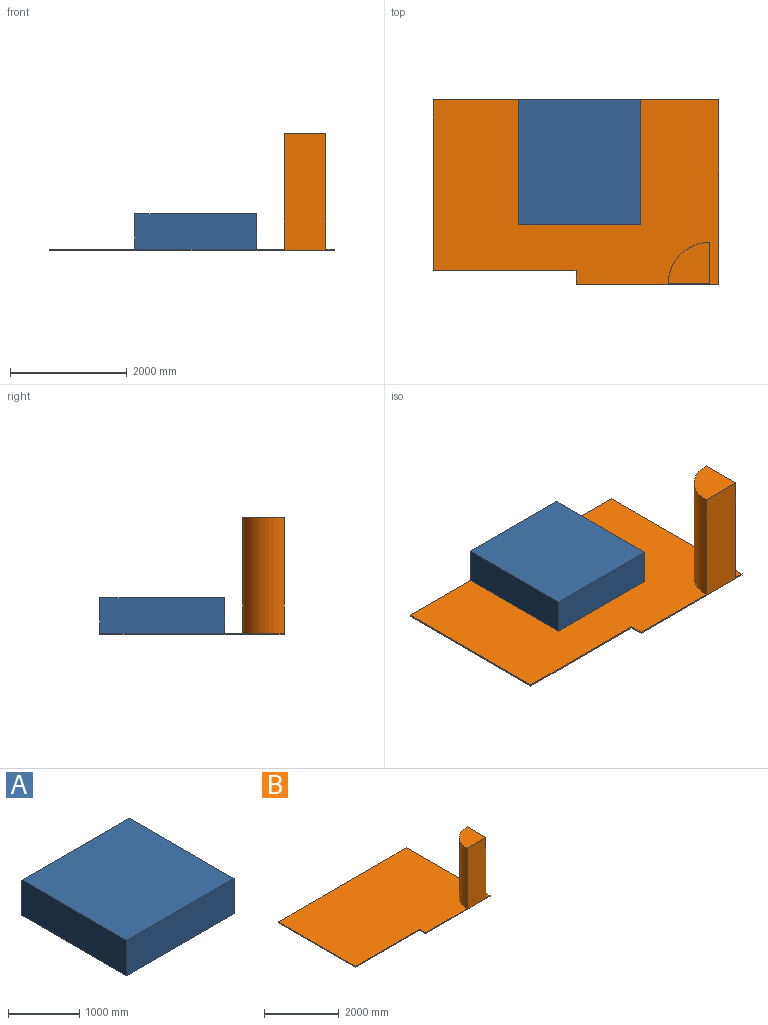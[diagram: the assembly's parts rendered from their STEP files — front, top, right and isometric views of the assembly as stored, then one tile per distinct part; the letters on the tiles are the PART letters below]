
ASSEMBLY  parts=2 mates=2
PART A: 6 faces, bbox 2133.6x2082.8x609.6 mm
  f0: plane 2133.6x609.6mm, normal (0,-1,0), area 1300642.6mm2, adj f1,f3,f4,f5
  f1: plane 2082.8x609.6mm, normal (1,0,0), area 1269674.9mm2, adj f0,f2,f4,f5
  f2: plane 2133.6x609.6mm, normal (0,1,0), area 1300642.6mm2, adj f1,f3,f4,f5
  f3: plane 2082.8x609.6mm, normal (-1,0,0), area 1269674.9mm2, adj f0,f2,f4,f5
  f4: plane 2133.6x2082.8mm, normal (0,0,1), area 4443862.1mm2, adj f0,f1,f2,f3
  f5: plane 2133.6x2082.8mm, normal (0,0,-1), area 4443862.1mm2, adj f0,f1,f2,f3
PART B: 11 faces, bbox 4876.8x3149.6x2006.2 mm
  f0: plane 2921x25mm, normal (-1,0,0), area 73025mm2, adj f1,f5,f6,f7
  f1: plane 2438.4x25mm, normal (0,-1,0), area 60960mm2, adj f0,f2,f6,f7
  f2: plane 228.6x25mm, normal (-1,0,0), area 5715mm2, adj f1,f3,f6,f7
  f3: plane 2438.4x2006.2mm, normal (0,-1,0), area 1469989.4mm2, adj f2,f4,f6,f7,f8,f9,f10
  f4: plane 3149.6x25mm, normal (1,0,0), area 78740mm2, adj f3,f5,f6,f7
  f5: plane 4876.8x25mm, normal (0,1,0), area 121920mm2, adj f0,f4,f6,f7
  f6: plane 4876.8x3149.6mm, normal (0,0,1), area 14405292.4mm2, adj f0,f1,f2,f3,f4,f5,f8,f9
  f7: plane 4876.8x3149.6mm, normal (0,0,-1), area 14802551mm2, adj f0,f1,f2,f3,f4,f5
  f8: plane 1981.2x711.2mm, normal (1,0,0), area 1409029.4mm2, adj f3,f6,f9,f10
  f9: cylinder r=711.2mm len=1981.2mm, axis (0,0,-1), area 2213298.3mm2, adj f3,f6,f8,f10
  f10: plane 711.2x711.2mm, normal (0,0,1), area 397258.7mm2, adj f3,f8,f9
PLACE A rot(axis=(0,0,-1),90deg) t=(2503.65,-1066.8,25)mm
PLACE B at identity fixed
MATE planar B.f6 <-> A.f5  axis (0,0,1) through (2430.86,-1483.18,25)mm
MATE planar B.f5 <-> A.f3  axis (0,1,0) through (2438.4,0,12.5)mm
